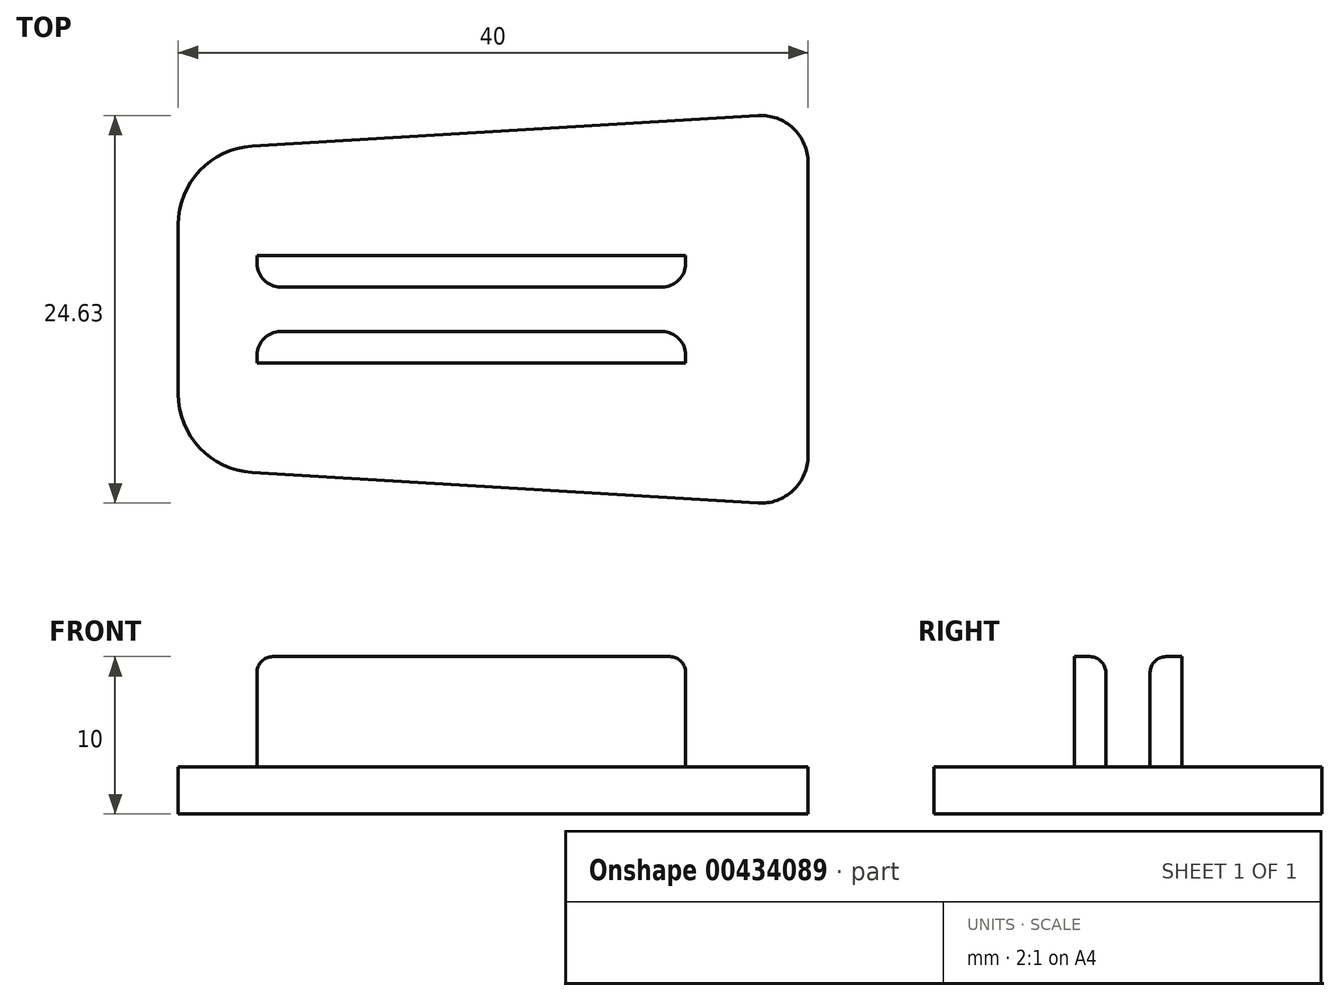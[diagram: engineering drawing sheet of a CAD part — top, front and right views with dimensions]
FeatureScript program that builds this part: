
annotation { "Feature Type Name" : "Feature", "Feature Type Description" : "" }
export const myFeature = defineFeature(function(context is Context, id is Id, definition is map)
    precondition{}
    {
        {
            var Q0;
            Q0=qCreatedBy(makeId("Top.planeOp"),FACE);
            var sketch = newSketch(context, id + "F0", { "sketchPlane" : qUnion([Q0])});
            skLineSegment(sketch, "E0.right", {"start": v(-7.71, 47.56) * mm, "end": v(-7.71, 22.56) * mm});
            skLineSegment(sketch, "E1", {"start": v(-81.04, 35.06) * mm, "end": v(-57.94, 35.06) * mm, "construction": true});
            skPoint(sketch, "E1.startSnap0", {"position": v(-65.71, 35.06) * mm});
            skLineSegment(sketch, "E2", {"start": v(-36.71, 62.88) * mm, "end": v(-36.71, 8.4) * mm, "construction": true});
            skPoint(sketch, "E2.startSnap0", {"position": v(-36.71, 51.56) * mm});
            skLineSegment(sketch, "E3.0", {"start": v(-42.71, 33.65) * mm, "end": v(-15.49, 33.65) * mm, "construction": true});
            skLineSegment(sketch, "E4.0", {"start": v(-42.71, 36.47) * mm, "end": v(-15.49, 36.47) * mm, "construction": true});
            skLineSegment(sketch, "E5.MirrorCS", {"start": v(-15.49, 38.47) * mm, "end": v(-15.49, 36.47) * mm, "construction": true});
            skLineSegment(sketch, "E6.top", {"start": v(-42.71, 38.47) * mm, "end": v(-15.49, 38.47) * mm, "construction": true});
            skLineSegment(sketch, "E6.right", {"start": v(-15.49, 36.47) * mm, "end": v(-15.49, 38.47) * mm, "construction": true});
            skLineSegment(sketch, "E7.top", {"start": v(-42.71, 33.65) * mm, "end": v(-15.49, 33.65) * mm});
            skLineSegment(sketch, "E8.bottom", {"start": v(-42.71, 38.47) * mm, "end": v(-15.49, 38.47) * mm});
            skLineSegment(sketch, "E8.top", {"start": v(-42.71, 36.47) * mm, "end": v(-15.49, 36.47) * mm});
            skLineSegment(sketch, "E8.right", {"start": v(-15.49, 38.47) * mm, "end": v(-15.49, 36.47) * mm});
            skLineSegment(sketch, "E9.trimOffspring", {"start": v(-15.49, 35.06) * mm, "end": v(7.2, 35.06) * mm, "construction": true});
            skLineSegment(sketch, "E10.top", {"start": v(-42.71, 31.65) * mm, "end": v(-15.49, 31.65) * mm});
            skLineSegment(sketch, "E10.right", {"start": v(-15.49, 33.65) * mm, "end": v(-15.49, 31.65) * mm});
            skLineSegment(sketch, "E11", {"start": v(-57.94, 35.06) * mm, "end": v(-15.49, 35.06) * mm, "construction": true});
            skPoint(sketch, "E0.bottom.start.orphan", {"position": v(-65.71, 51.56) * mm});
            skPoint(sketch, "E12.orphan", {"position": v(-65.71, 18.56) * mm});
            skPoint(sketch, "E13.orphan", {"position": v(-57.94, 26.23) * mm});
            skPoint(sketch, "E14.orphan", {"position": v(-57.94, 42.1) * mm});
            skPoint(sketch, "E15.orphan", {"position": v(-15.49, 42.1) * mm});
            skPoint(sketch, "E16.orphan", {"position": v(-15.49, 26.23) * mm});
            skLineSegment(sketch, "E17.trimOffspring", {"start": v(-15.49, 33.65) * mm, "end": v(-15.49, 31.65) * mm, "construction": true});
            skLineSegment(sketch, "E18", {"start": v(-47.71, 45.15) * mm, "end": v(-7.71, 47.56) * mm});
            skPoint(sketch, "E18.endSnap0", {"position": v(-4.15, 47.56) * mm});
            skLineSegment(sketch, "E19", {"start": v(-47.71, 24.98) * mm, "end": v(-7.71, 22.56) * mm});
            skPoint(sketch, "E20.orphan", {"position": v(-7.71, 51.56) * mm});
            skPoint(sketch, "E21.trimOffspring.end.orphan", {"position": v(7.2, 47.56) * mm});
            skPoint(sketch, "E22.MirrorCS.start.orphan", {"position": v(-15.49, 47.56) * mm});
            skPoint(sketch, "E23.orphan", {"position": v(7.2, 22.56) * mm});
            skPoint(sketch, "E24.0.start.orphan", {"position": v(-15.49, 22.56) * mm});
            skPoint(sketch, "E25.orphan", {"position": v(-65.71, 20.56) * mm});
            skPoint(sketch, "E26.MirrorCS.end.orphan", {"position": v(-7.71, 18.56) * mm});
            skPoint(sketch, "E27.orphan", {"position": v(-65.71, 49.56) * mm});
            skLineSegment(sketch, "E28.0", {"start": v(-47.71, 45.15) * mm, "end": v(-47.71, 24.98) * mm});
            skPoint(sketch, "E10.left.end.orphan", {"position": v(-57.94, 31.65) * mm});
            skPoint(sketch, "E10.left.start.orphan", {"position": v(-57.94, 33.65) * mm});
            skPoint(sketch, "E8.left.end.orphan", {"position": v(-57.94, 36.47) * mm});
            skPoint(sketch, "E8.left.start.orphan", {"position": v(-57.94, 38.47) * mm});
            skLineSegment(sketch, "E29", {"start": v(-42.71, 31.65) * mm, "end": v(-42.71, 33.65) * mm});
            skLineSegment(sketch, "E30", {"start": v(-42.71, 38.47) * mm, "end": v(-42.71, 36.47) * mm});
            skSolve(sketch);
        }
        {
            var Q0;
            Q0=makeQuery(id+"F0.imprint","IMPRINT",FACE,{"disambiguationData":[TD([[makeQuery(id+"F0.imprint","IMPRINT",EDGE,{"derivedFrom":sQuery(id+"F0.wireOp",EDGE,"E0.right")}),-1.0]])]});
            extrude(context, id + "F1", {"entities" : qUnion([Q0]), "depth" : 3 * mm, "offsetDistance" : 25 * mm});
        }
        {
            var Q0;
            Q0=makeQuery(id+"F0.imprint","IMPRINT",FACE,{"disambiguationData":[TD([[makeQuery(id+"F0.imprint","IMPRINT",EDGE,{"derivedFrom":sQuery(id+"F0.wireOp",EDGE,"E7.top")}),-1.0]])]});
            var Q1;
            Q1=makeQuery(id+"F0.imprint","IMPRINT",FACE,{"disambiguationData":[TD([[makeQuery(id+"F0.imprint","IMPRINT",EDGE,{"derivedFrom":sQuery(id+"F0.wireOp",EDGE,"E8.bottom")}),-1.0]])]});
            extrude(context, id + "F2", {"entities" : qUnion([Q0, Q1]), "operationType" : NewBodyOperationType.ADD, "depth" : 10 * mm, "offsetDistance" : 25 * mm});
        }
        {
            var Q0;
            Q0=makeQuery(id+"F2.opExtrude","SWEPT_EDGE",EDGE,{"disambiguationData":[OSD([sQuery(id+"F0.wireOp",EDGE,"E8.top"),sQuery(id+"F0.wireOp",EDGE,"E8.left")])]});
            var Q1;
            Q1=makeQuery(id+"F2.opExtrude","SWEPT_EDGE",EDGE,{"disambiguationData":[OSD([sQuery(id+"F0.wireOp",EDGE,"E7.top"),sQuery(id+"F0.wireOp",EDGE,"E10.left")])]});
            var Q2;
            Q2=makeQuery(id+"F2.opExtrude","SWEPT_EDGE",EDGE,{"disambiguationData":[OSD([sQuery(id+"F0.wireOp",EDGE,"E8.top"),sQuery(id+"F0.wireOp",EDGE,"E8.right")])]});
            var Q3;
            Q3=makeQuery(id+"F2.opExtrude","SWEPT_EDGE",EDGE,{"disambiguationData":[OSD([sQuery(id+"F0.wireOp",EDGE,"E7.top"),sQuery(id+"F0.wireOp",EDGE,"E10.right")])]});
            fillet(context, id + "F3", {"entities" : qUnion([Q0, Q1, Q2, Q3]), "radius" : 1.5 * mm, "tangentPropagation" : true, "allowEdgeOverflow" : false});
        }
        {
            var Q0;
            Q0=makeQuery(id+"F2.opExtrude","CAP_EDGE",EDGE,{"disambiguationData":[OSD([sQuery(id+"F0.wireOp",EDGE,"E8.top")])],"isStart":false});
            var Q1;
            Q1=makeQuery(id+"F2.opExtrude","CAP_EDGE",EDGE,{"disambiguationData":[OSD([sQuery(id+"F0.wireOp",EDGE,"E7.top")])],"isStart":false});
            fillet(context, id + "F4", {"entities" : qUnion([Q0, Q1]), "radius" : 1 * mm, "tangentPropagation" : true, "allowEdgeOverflow" : false});
        }
        {
            var Q0;
            Q0=makeQuery(id+"F1.opExtrude","SWEPT_EDGE",EDGE,{"disambiguationData":[OSD([sQuery(id+"F0.wireOp",EDGE,"E0.bottom"),sQuery(id+"F0.wireOp",EDGE,"E0.right")])]});
            var Q1;
            Q1=makeQuery(id+"F1.opExtrude","SWEPT_EDGE",EDGE,{"disambiguationData":[OSD([sQuery(id+"F0.wireOp",EDGE,"E0.top"),sQuery(id+"F0.wireOp",EDGE,"E0.left")])]});
            var Q2;
            Q2=makeQuery(id+"F1.opExtrude","SWEPT_EDGE",EDGE,{"disambiguationData":[OSD([sQuery(id+"F0.wireOp",EDGE,"E0.bottom"),sQuery(id+"F0.wireOp",EDGE,"E0.left")])]});
            var Q3;
            Q3=makeQuery(id+"F1.opExtrude","SWEPT_EDGE",EDGE,{"disambiguationData":[OSD([sQuery(id+"F0.wireOp",EDGE,"E0.top"),sQuery(id+"F0.wireOp",EDGE,"E0.right")])]});
            fillet(context, id + "F5", {"entities" : qUnion([Q0, Q1, Q2, Q3]), "radius" : 3 * mm, "tangentPropagation" : true, "allowEdgeOverflow" : false});
        }
        {
            var Q0;
            Q0=makeQuery(id+"F1.opExtrude","SWEPT_EDGE",EDGE,{"disambiguationData":[OSD([sQuery(id+"F0.wireOp",EDGE,"E18"),sQuery(id+"F0.wireOp",EDGE,"E28.0")])]});
            var Q1;
            Q1=makeQuery(id+"F1.opExtrude","SWEPT_EDGE",EDGE,{"disambiguationData":[OSD([sQuery(id+"F0.wireOp",EDGE,"E19"),sQuery(id+"F0.wireOp",EDGE,"E28.0")])]});
            fillet(context, id + "F6", {"entities" : qUnion([Q0, Q1]), "radius" : 5 * mm, "tangentPropagation" : true, "allowEdgeOverflow" : false});
        }
    });
